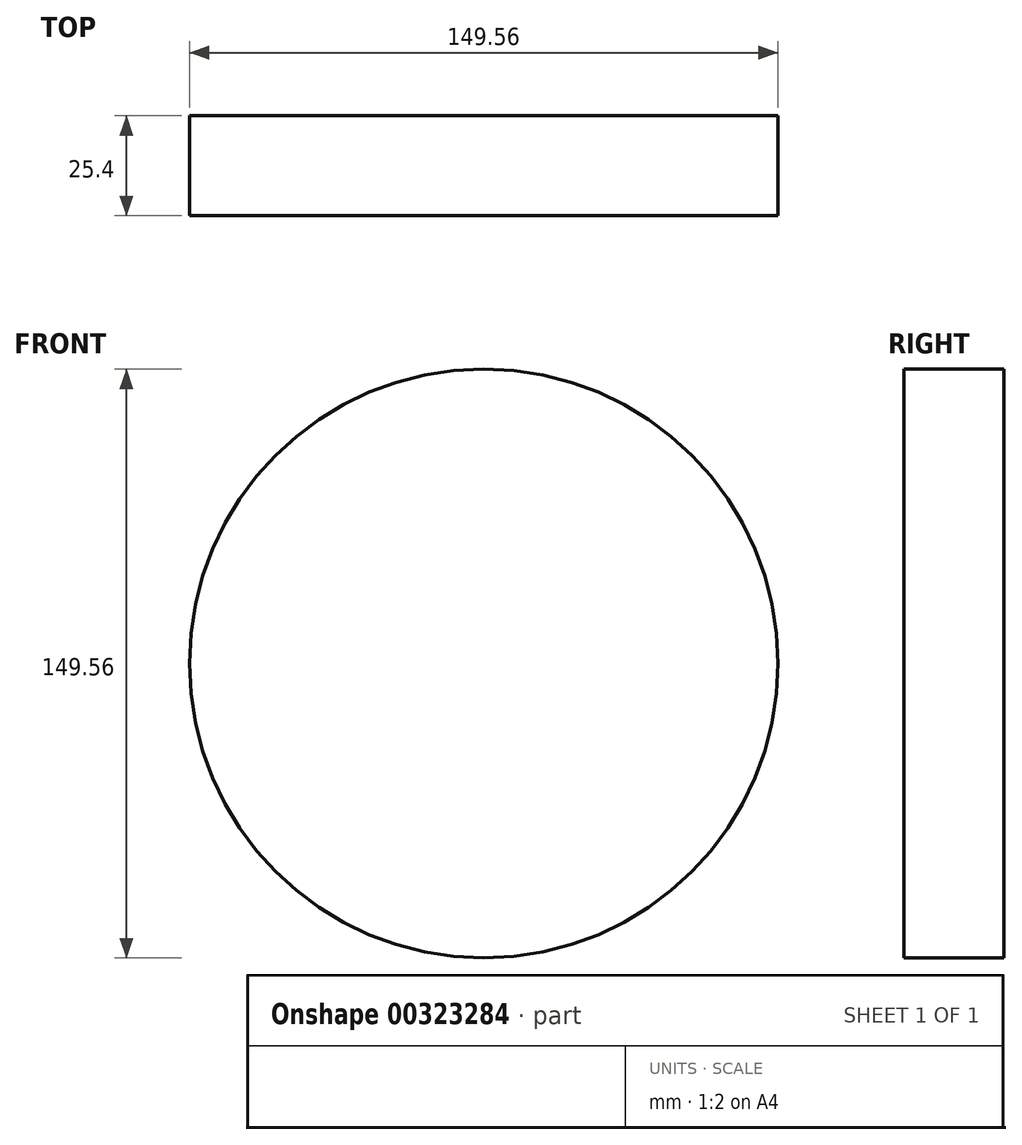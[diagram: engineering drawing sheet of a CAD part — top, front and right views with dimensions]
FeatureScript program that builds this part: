
annotation { "Feature Type Name" : "Feature", "Feature Type Description" : "" }
export const myFeature = defineFeature(function(context is Context, id is Id, definition is map)
    precondition{}
    {
        {
            var Q0;
            Q0=qCreatedBy(makeId("Front.planeOp"),FACE);
            var sketch = newSketch(context, id + "F0", { "sketchPlane" : qUnion([Q0])});
            skCircle(sketch, "E0", {"center": v(0, 0) * mm, "radius": 74.78 * mm});
            skSolve(sketch);
        }
        {
            var Q0;
            Q0 = qSketchRegion(id + "F0", true);
            extrude(context, id + "F1", {"entities" : qUnion([Q0]), "endBound" : BoundingType.SYMMETRIC, "oppositeDirection" : true, "depth" : 25.4 * mm});
        }
    });
